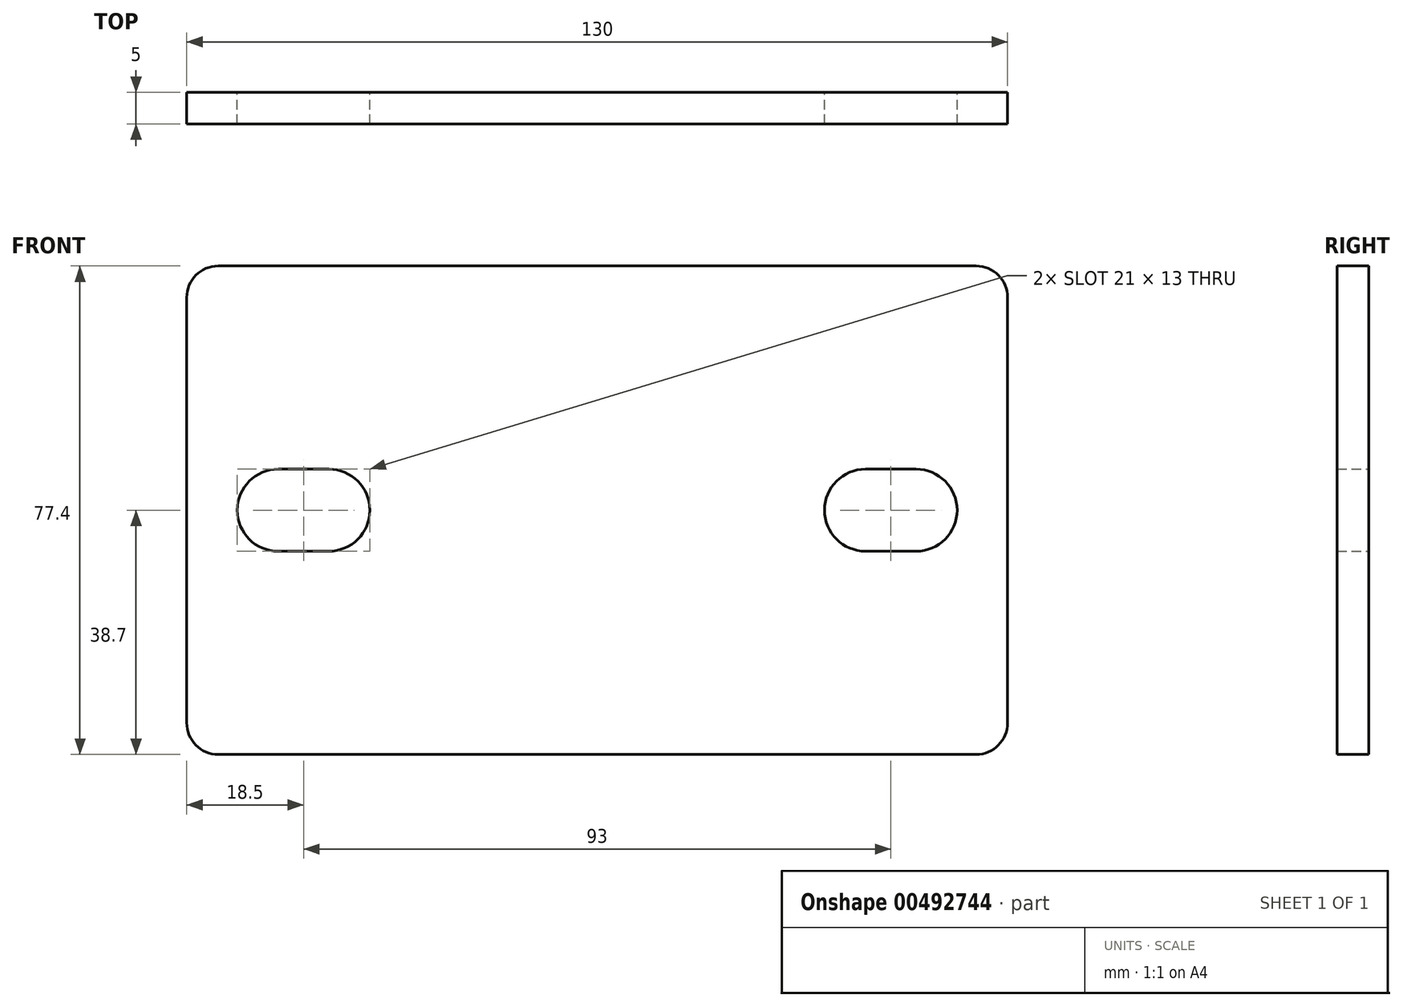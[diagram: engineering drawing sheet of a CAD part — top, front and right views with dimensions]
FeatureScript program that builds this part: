
annotation { "Feature Type Name" : "Feature", "Feature Type Description" : "" }
export const myFeature = defineFeature(function(context is Context, id is Id, definition is map)
    precondition{}
    {
        {
            var Q0;
            Q0=qCreatedBy(makeId("Front.planeOp"),FACE);
            var sketch = newSketch(context, id + "F0", { "sketchPlane" : qUnion([Q0])});
            skLineSegment(sketch, "E0.bottom", {"start": v(65, 38.7) * mm, "end": v(-65, 38.7) * mm});
            skLineSegment(sketch, "E0.top", {"start": v(65, -38.7) * mm, "end": v(-65, -38.7) * mm});
            skLineSegment(sketch, "E0.left", {"start": v(65, 38.7) * mm, "end": v(65, -38.7) * mm});
            skLineSegment(sketch, "E0.right", {"start": v(-65, 38.7) * mm, "end": v(-65, -38.7) * mm});
            skPoint(sketch, "E0.middle", {"position": v(0, 0) * mm});
            skLineSegment(sketch, "E1.bottom", {"start": v(-42.5, -6.5) * mm, "end": v(-50.5, -6.5) * mm});
            skLineSegment(sketch, "E1.top", {"start": v(-42.5, 6.5) * mm, "end": v(-50.5, 6.5) * mm});
            skLineSegment(sketch, "E1.left", {"start": v(-36, 0) * mm, "end": v(-36, 0) * mm});
            skLineSegment(sketch, "E1.right", {"start": v(-57, 0) * mm, "end": v(-57, 0) * mm});
            skPoint(sketch, "E1.middle", {"position": v(-46.5, 0) * mm});
            skPoint(sketch, "E1.middle.positionSnap0", {"position": v(-65, 0) * mm});
            skPoint(sketch, "E1.centerSnap0", {"position": v(-65, 0) * mm});
            skPoint(sketch, "E2.visualSharp", {"position": v(-36, 6.5) * mm});
            skArc(sketch, "E2.filletArc", {"start": v(-36, 0) * mm, "mid": v(-37.9, 4.6) * mm, "end": v(-42.5, 6.5) * mm});
            skPoint(sketch, "E3.visualSharp", {"position": v(-36, -6.5) * mm});
            skArc(sketch, "E3.filletArc", {"start": v(-42.5, -6.5) * mm, "mid": v(-37.9, -4.6) * mm, "end": v(-36, 0) * mm});
            skPoint(sketch, "E4.visualSharp", {"position": v(-57, 6.5) * mm});
            skArc(sketch, "E4.filletArc", {"start": v(-50.5, 6.5) * mm, "mid": v(-55.1, 4.6) * mm, "end": v(-57, 0) * mm});
            skPoint(sketch, "E5.visualSharp", {"position": v(-57, -6.5) * mm});
            skArc(sketch, "E5.filletArc", {"start": v(-57, 0) * mm, "mid": v(-55.1, -4.6) * mm, "end": v(-50.5, -6.5) * mm});
            skPoint(sketch, "E6.MirrorP", {"position": v(57, -6.5) * mm});
            skPoint(sketch, "E7.MirrorP", {"position": v(46.5, 0) * mm});
            skPoint(sketch, "E8.MirrorP", {"position": v(36, 6.5) * mm});
            skPoint(sketch, "E9.MirrorP", {"position": v(36, -6.5) * mm});
            skArc(sketch, "E10.MirrorCS", {"start": v(57, 0) * mm, "mid": v(55.1, -4.6) * mm, "end": v(50.5, -6.5) * mm});
            skArc(sketch, "E11.MirrorCS", {"start": v(50.5, 6.5) * mm, "mid": v(55.1, 4.6) * mm, "end": v(57, 0) * mm});
            skPoint(sketch, "E12.MirrorP", {"position": v(57, 6.5) * mm});
            skArc(sketch, "E13.MirrorCS", {"start": v(42.5, -6.5) * mm, "mid": v(37.9, -4.6) * mm, "end": v(36, 0) * mm});
            skArc(sketch, "E14.MirrorCS", {"start": v(36, 0) * mm, "mid": v(37.9, 4.6) * mm, "end": v(42.5, 6.5) * mm});
            skLineSegment(sketch, "E15.MirrorCS", {"start": v(42.5, -6.5) * mm, "end": v(50.5, -6.5) * mm});
            skLineSegment(sketch, "E16.MirrorCS", {"start": v(42.5, 6.5) * mm, "end": v(50.5, 6.5) * mm});
            skSolve(sketch);
        }
        {
            var Q0;
            Q0=makeQuery(id+"F0.imprint","IMPRINT",FACE,{"disambiguationData":[TD([[makeQuery(id+"F0.imprint","IMPRINT",EDGE,{"derivedFrom":sQuery(id+"F0.wireOp",EDGE,"E0.bottom")}),1.0]])]});
            extrude(context, id + "F1", {"entities" : qUnion([Q0]), "depth" : 5 * mm});
        }
        {
            var Q0;
            Q0=makeQuery(id+"F1.opExtrude","SWEPT_EDGE",EDGE,{"disambiguationData":[OSD([sQuery(id+"F0.wireOp",EDGE,"E0.bottom"),sQuery(id+"F0.wireOp",EDGE,"E0.left")])]});
            var Q1;
            Q1=makeQuery(id+"F1.opExtrude","SWEPT_EDGE",EDGE,{"disambiguationData":[OSD([sQuery(id+"F0.wireOp",EDGE,"E0.top"),sQuery(id+"F0.wireOp",EDGE,"E0.left")])]});
            var Q2;
            Q2=makeQuery(id+"F1.opExtrude","SWEPT_EDGE",EDGE,{"disambiguationData":[OSD([sQuery(id+"F0.wireOp",EDGE,"E0.top"),sQuery(id+"F0.wireOp",EDGE,"E0.right")])]});
            var Q3;
            Q3=makeQuery(id+"F1.opExtrude","SWEPT_EDGE",EDGE,{"disambiguationData":[OSD([sQuery(id+"F0.wireOp",EDGE,"E0.bottom"),sQuery(id+"F0.wireOp",EDGE,"E0.right")])]});
            fillet(context, id + "F2", {"entities" : qUnion([Q0, Q1, Q2, Q3]), "radius" : 5 * mm, "tangentPropagation" : true, "allowEdgeOverflow" : false});
        }
    });
